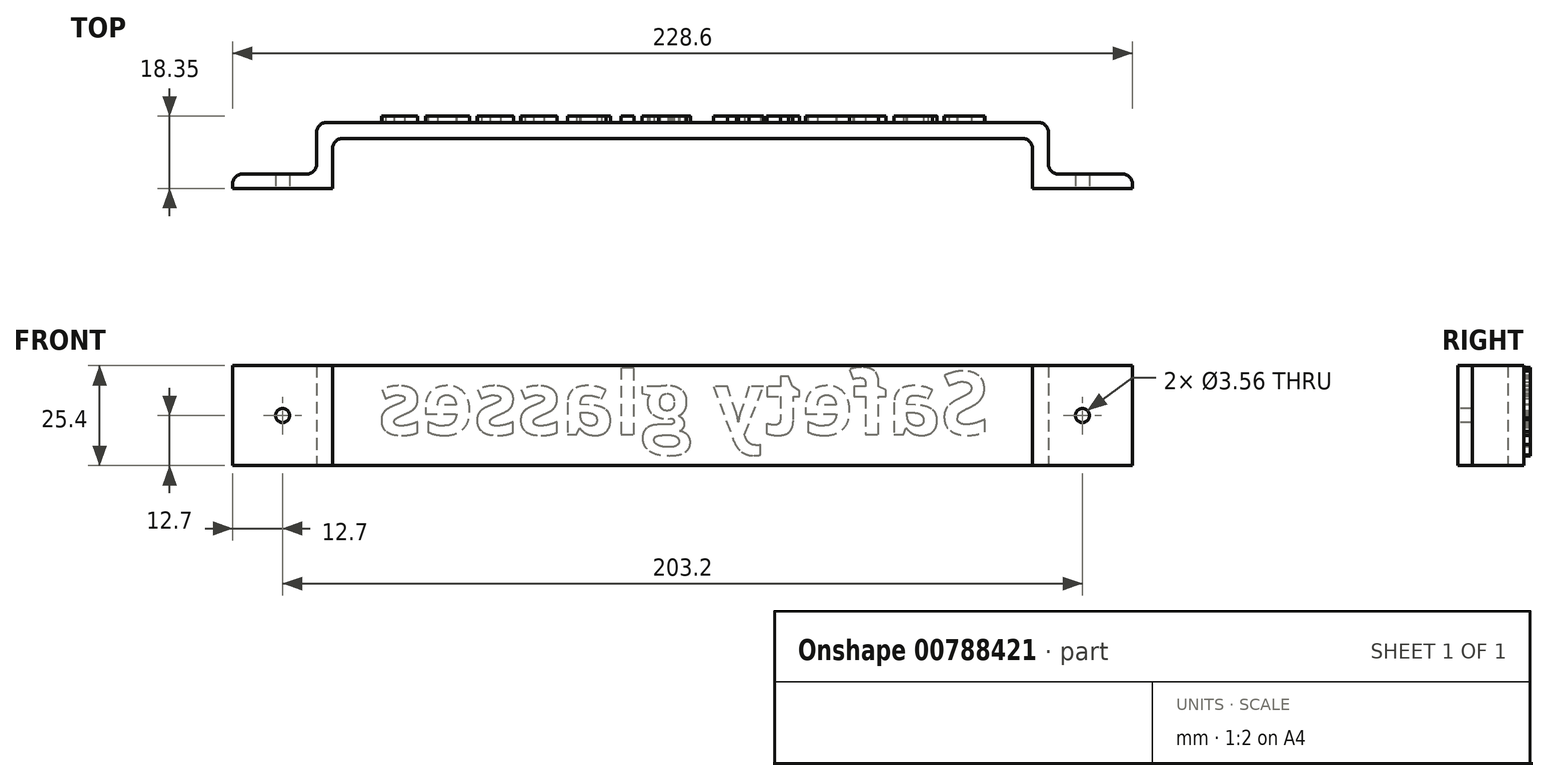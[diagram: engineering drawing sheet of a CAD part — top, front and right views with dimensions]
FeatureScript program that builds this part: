
annotation { "Feature Type Name" : "Feature", "Feature Type Description" : "" }
export const myFeature = defineFeature(function(context is Context, id is Id, definition is map)
    precondition{}
    {
        {
            var Q0;
            Q0=qCreatedBy(makeId("Top.planeOp"),FACE);
            var sketch = newSketch(context, id + "F0", { "sketchPlane" : qUnion([Q0])});
            skLineSegment(sketch, "E0.bottom", {"start": v(-59.36, 3.65) * mm, "end": v(-43.1, 3.65) * mm});
            skLineSegment(sketch, "E0.top", {"start": v(-61.9, 0) * mm, "end": v(-43.02, 0) * mm});
            skLineSegment(sketch, "E0.left", {"start": v(-61.9, 1.11) * mm, "end": v(-61.9, 0) * mm});
            skLineSegment(sketch, "E0.right", {"start": v(-43.02, 4.57) * mm, "end": v(-43.02, 0) * mm});
            skLineSegment(sketch, "E1.bottom", {"start": v(147.9, 3.65) * mm, "end": v(164.16, 3.65) * mm});
            skLineSegment(sketch, "E1.top", {"start": v(147.82, 0) * mm, "end": v(166.7, 0) * mm});
            skLineSegment(sketch, "E1.left", {"start": v(147.82, 4.57) * mm, "end": v(147.82, 0) * mm});
            skLineSegment(sketch, "E1.right", {"start": v(166.7, 1.11) * mm, "end": v(166.7, 0) * mm});
            skLineSegment(sketch, "E2.bottom", {"start": v(-43.02, 0) * mm, "end": v(-36.5, 0) * mm});
            skLineSegment(sketch, "E2.top", {"start": v(-38.02, 16.76) * mm, "end": v(142.82, 16.76) * mm});
            skLineSegment(sketch, "E2.left", {"start": v(-40.56, 6.2) * mm, "end": v(-40.56, 14.22) * mm});
            skLineSegment(sketch, "E2.right", {"start": v(145.36, 6.2) * mm, "end": v(145.36, 14.22) * mm});
            skLineSegment(sketch, "E3.0", {"start": v(141.3, 0) * mm, "end": v(141.3, 10.16) * mm});
            skLineSegment(sketch, "E3.1", {"start": v(-33.96, 12.7) * mm, "end": v(138.76, 12.7) * mm});
            skLineSegment(sketch, "E3.2", {"start": v(-36.5, 0) * mm, "end": v(-36.5, 10.16) * mm});
            skLineSegment(sketch, "E4.trimOffspring", {"start": v(141.3, 0) * mm, "end": v(147.82, 0) * mm});
            skPoint(sketch, "E5.visualSharp", {"position": v(145.36, 16.76) * mm});
            skArc(sketch, "E5.filletArc", {"start": v(145.36, 14.22) * mm, "mid": v(144.62, 16.02) * mm, "end": v(142.82, 16.76) * mm});
            skPoint(sketch, "E6.visualSharp", {"position": v(-40.56, 16.76) * mm});
            skArc(sketch, "E6.filletArc", {"start": v(-38.02, 16.76) * mm, "mid": v(-39.82, 16.02) * mm, "end": v(-40.56, 14.22) * mm});
            skArc(sketch, "E7.filletArc", {"start": v(-43.1, 3.65) * mm, "mid": v(-41.3, 4.4) * mm, "end": v(-40.56, 6.2) * mm});
            skPoint(sketch, "E8.visualSharp", {"position": v(141.3, 12.7) * mm});
            skArc(sketch, "E8.filletArc", {"start": v(141.3, 10.16) * mm, "mid": v(140.56, 11.96) * mm, "end": v(138.76, 12.7) * mm});
            skPoint(sketch, "E9.visualSharp", {"position": v(-36.5, 12.7) * mm});
            skArc(sketch, "E9.filletArc", {"start": v(-33.96, 12.7) * mm, "mid": v(-35.76, 11.96) * mm, "end": v(-36.5, 10.16) * mm});
            skArc(sketch, "E10.filletArc", {"start": v(145.36, 6.2) * mm, "mid": v(146.1, 4.4) * mm, "end": v(147.9, 3.65) * mm});
            skPoint(sketch, "E11.visualSharp", {"position": v(166.7, 3.65) * mm});
            skArc(sketch, "E11.filletArc", {"start": v(166.7, 1.11) * mm, "mid": v(165.96, 2.9) * mm, "end": v(164.16, 3.65) * mm});
            skPoint(sketch, "E12.visualSharp", {"position": v(-61.9, 3.65) * mm});
            skArc(sketch, "E12.filletArc", {"start": v(-59.36, 3.65) * mm, "mid": v(-61.16, 2.9) * mm, "end": v(-61.9, 1.11) * mm});
            skSolve(sketch);
        }
        {
            var Q0;
            Q0=makeQuery(id+"F0.imprint","IMPRINT",FACE,{"disambiguationData":[TD([[makeQuery(id+"F0.imprint","IMPRINT",EDGE,{"derivedFrom":sQuery(id+"F0.wireOp",EDGE,"E0.bottom")}),-1.0]])]});
            var Q1;
            {var subQ4=sQuery(id+"F0.wireOp",EDGE,"E1.bottom");Q1=makeQuery(id+"F0.imprint","IMPRINT",FACE,{"disambiguationData":[TD([[makeQuery(id+"F0.imprint","IMPRINT",EDGE,{"derivedFrom":subQ4}),-1.0]])]});}
            var Q2;
            {var subQ3=sQuery(id+"F0.wireOp",EDGE,"E2.bottom");Q2=makeQuery(id+"F0.imprint","IMPRINT",FACE,{"disambiguationData":[TD([[makeQuery(id+"F0.imprint","IMPRINT",EDGE,{"derivedFrom":subQ3}),1.0]])]});}
            extrude(context, id + "F1", {"entities" : qUnion([Q0, Q1, Q2]), "depth" : 25.4 * mm, "offsetDistance" : 25.4 * mm});
        }
        {
            var Q0;
            Q0=makeQuery(id+"F1.opExtrude","SWEPT_FACE",FACE,{"disambiguationData":[OSD([sQuery(id+"F0.wireOp",EDGE,"E0.top"),sQuery(id+"F0.wireOp",EDGE,"E2.bottom")])]});
            var sketch = newSketch(context, id + "F2", { "sketchPlane" : qUnion([Q0])});
            skPoint(sketch, "E13", {"position": v(-49.2, 25.4) * mm});
            skPoint(sketch, "E14", {"position": v(-36.5, 12.7) * mm});
            skPoint(sketch, "E15", {"position": v(-61.9, 12.7) * mm});
            skPoint(sketch, "E16", {"position": v(-49.2, 0) * mm});
            skLineSegment(sketch, "E17", {"start": v(-61.9, 12.7) * mm, "end": v(-36.5, 12.7) * mm});
            skPoint(sketch, "E18", {"position": v(-49.2, 12.7) * mm});
            skLineSegment(sketch, "E19", {"start": v(-36.5, 12.7) * mm, "end": v(166.7, 12.7) * mm});
            skLineSegment(sketch, "E20", {"start": v(166.7, 12.7) * mm, "end": v(154, 12.7) * mm});
            skLineSegment(sketch, "E21", {"start": v(-61.9, 12.7) * mm, "end": v(-49.2, 12.7) * mm});
            skSolve(sketch);
        }
        {
            var Q0;
            Q0=sQuery(id+"F2.wireOp",VERTEX,"E18");
            var Q1;
            Q1=sQuery(id+"F2.wireOp",VERTEX,"E20.end");
            var Q2;
            Q2=makeQuery(id+"F1.opExtrude","SWEPT_BODY",BODY,{"disambiguationData":[OSD([sQuery(id+"F0.wireOp",EDGE,"E0.bottom"),sQuery(id+"F0.wireOp",EDGE,"E0.top"),sQuery(id+"F0.wireOp",EDGE,"E0.left"),sQuery(id+"F0.wireOp",EDGE,"E1.bottom"),sQuery(id+"F0.wireOp",EDGE,"E1.top"),sQuery(id+"F0.wireOp",EDGE,"E1.right"),sQuery(id+"F0.wireOp",EDGE,"E2.bottom"),sQuery(id+"F0.wireOp",EDGE,"E2.top"),sQuery(id+"F0.wireOp",EDGE,"E2.left"),sQuery(id+"F0.wireOp",EDGE,"E2.right"),sQuery(id+"F0.wireOp",EDGE,"E3.0"),sQuery(id+"F0.wireOp",EDGE,"E3.1"),sQuery(id+"F0.wireOp",EDGE,"E3.2"),sQuery(id+"F0.wireOp",EDGE,"E4.trimOffspring"),sQuery(id+"F0.wireOp",EDGE,"E5.filletArc"),sQuery(id+"F0.wireOp",EDGE,"E6.filletArc"),sQuery(id+"F0.wireOp",EDGE,"E7.filletArc"),sQuery(id+"F0.wireOp",EDGE,"E8.filletArc"),sQuery(id+"F0.wireOp",EDGE,"E9.filletArc"),sQuery(id+"F0.wireOp",EDGE,"E10.filletArc"),sQuery(id+"F0.wireOp",EDGE,"E11.filletArc"),sQuery(id+"F0.wireOp",EDGE,"E12.filletArc")])]});
            hole(context, id + "F3", {"style" : HoleStyle.C_SINK, "endStyle" : HoleEndStyle.THROUGH, "holeDiameter" : 3.56 * mm, "cSinkDiameter" : 3.56 * mm, "cSinkAngle" : 90 * degree, "majorDiameter" : 6.35 * mm, "isTappedThrough" : true, "tappedDepth" : 12.7 * mm, "tapClearance" : 3, "locations" : qUnion([Q0, Q1]), "scope" : qUnion([Q2])});
        }
        {
            var Q0;
            Q0=makeQuery(id+"F1.opExtrude","SWEPT_FACE",FACE,{"disambiguationData":[OSD([sQuery(id+"F0.wireOp",EDGE,"E2.top")])]});
            var sketch = newSketch(context, id + "F4", { "sketchPlane" : qUnion([Q0])});
            skText(sketch, "E22", { "text": "Safety glasses", "fontName": "OpenSans-Bold.ttf"});
            skPoint(sketch, "E23", {"position": v(-130.29, 23.95) * mm});
            const initialGuessF4  = {"E22": [-0.13029, 0.00787, 1, 0, 0.01608]};
            skSetInitialGuess(sketch, initialGuessF4);
            skSolve(sketch);
        }
        {
            var Q0;
            Q0=qSketchRegion(id+"F4",true);
            extrude(context, id + "F5", {"entities" : qUnion([Q0]), "operationType" : NewBodyOperationType.ADD, "depth" : 1.59 * mm, "offsetDistance" : 25.4 * mm});
        }
    });
